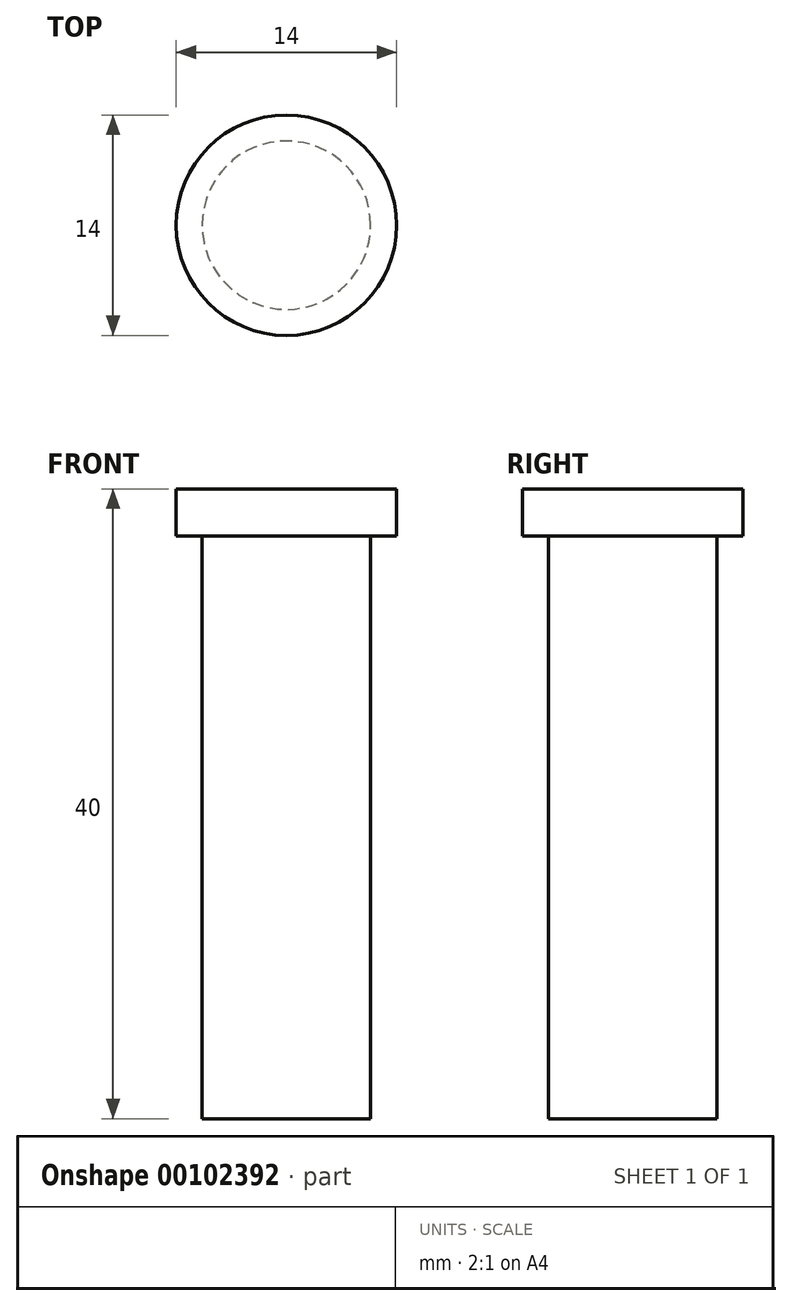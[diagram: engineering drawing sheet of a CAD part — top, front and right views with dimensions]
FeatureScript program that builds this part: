
annotation { "Feature Type Name" : "Feature", "Feature Type Description" : "" }
export const myFeature = defineFeature(function(context is Context, id is Id, definition is map)
    precondition{}
    {
        {
            var Q0;
            Q0=qCreatedBy(makeId("Front.planeOp"),FACE);
            var sketch = newSketch(context, id + "F0", { "sketchPlane" : qUnion([Q0])});
            skLineSegment(sketch, "E0", {"start": v(0, 0) * mm, "end": v(0, 47.7) * mm, "construction": true});
            skLineSegment(sketch, "E1", {"start": v(0, 0) * mm, "end": v(0, 40) * mm});
            skLineSegment(sketch, "E2", {"start": v(0, 40) * mm, "end": v(7, 40) * mm});
            skLineSegment(sketch, "E3", {"start": v(7, 40) * mm, "end": v(7, 37) * mm});
            skLineSegment(sketch, "E4", {"start": v(7, 37) * mm, "end": v(5.35, 37) * mm});
            skLineSegment(sketch, "E5", {"start": v(5.35, 37) * mm, "end": v(5.35, 0) * mm});
            skLineSegment(sketch, "E6", {"start": v(5.35, 0) * mm, "end": v(0, 0) * mm});
            skSolve(sketch);
        }
        {
            var Q0;
            Q0=makeQuery(id+"F0.imprint","IMPRINT",FACE,{"disambiguationData":[TD([[makeQuery(id+"F0.imprint","IMPRINT",EDGE,{"derivedFrom":sQuery(id+"F0.wireOp",EDGE,"JUl5yCzI-7aLU-8VHB-0Ogx-aDHex2DSwL5c")}),-1.0]])]});
            var Q1;
            Q1=makeQuery(id+"F0.imprint","IMPRINT",FACE,{"disambiguationData":[TD([[makeQuery(id+"F0.imprint","IMPRINT",EDGE,{"derivedFrom":sQuery(id+"F0.wireOp",EDGE,"E1")}),-1.0]])]});
            var Q2;
            Q2=sQuery(id+"F0.wireOp",EDGE,"E0");
            revolve(context, id + "F1", {"entities" : qUnion([Q0, Q1]), "axis" : qUnion([Q2]), "revolveType" : RevolveType.FULL});
        }
    });
